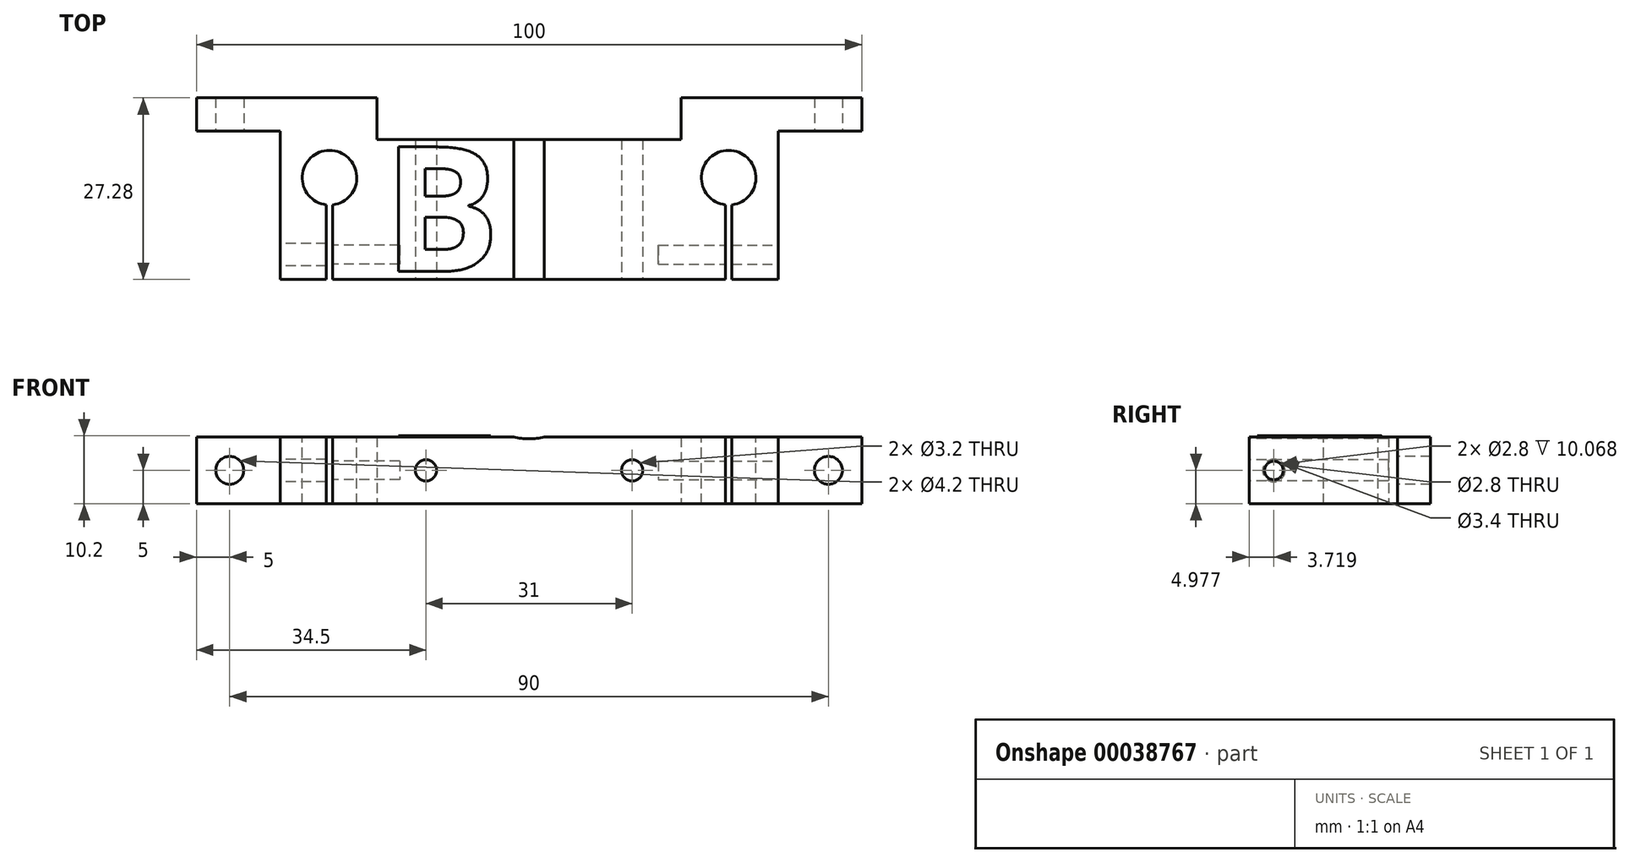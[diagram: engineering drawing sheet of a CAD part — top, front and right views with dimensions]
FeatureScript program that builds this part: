
annotation { "Feature Type Name" : "Feature", "Feature Type Description" : "" }
export const myFeature = defineFeature(function(context is Context, id is Id, definition is map)
    precondition{}
    {
        {
            var Q0;
            Q0=qCreatedBy(makeId("Top.planeOp"),FACE);
            var sketch = newSketch(context, id + "F0", { "sketchPlane" : qUnion([Q0])});
            skLineSegment(sketch, "E0", {"start": v(0, -13.82) * mm, "end": v(-37.44, -13.82) * mm});
            skLineSegment(sketch, "E1", {"start": v(-37.44, -13.82) * mm, "end": v(-37.44, 8.46) * mm});
            skLineSegment(sketch, "E2", {"start": v(-37.44, 8.46) * mm, "end": v(-50, 8.46) * mm});
            skLineSegment(sketch, "E3", {"start": v(-50, 8.46) * mm, "end": v(-50, 13.46) * mm});
            skLineSegment(sketch, "E4", {"start": v(-50, 13.46) * mm, "end": v(-22.87, 13.46) * mm});
            skLineSegment(sketch, "E5", {"start": v(-22.87, 13.46) * mm, "end": v(-22.87, 7.18) * mm});
            skLineSegment(sketch, "E6", {"start": v(-22.87, 7.18) * mm, "end": v(0, 7.18) * mm});
            skLineSegment(sketch, "E7", {"start": v(0, 7.18) * mm, "end": v(0, -13.82) * mm});
            skSolve(sketch);
        }
        {
            var Q0;
            Q0=qSketchRegion(id+"F0",true);
            extrude(context, id + "F1", {"entities" : qUnion([Q0]), "depth" : 10 * mm});
        }
        {
            var Q0;
            Q0=makeQuery(id+"F1.opExtrude","SWEPT_FACE",FACE,{"disambiguationData":[OSD([sQuery(id+"F0.wireOp",EDGE,"E0")])]});
            var sketch = newSketch(context, id + "F2", { "sketchPlane" : qUnion([Q0])});
            skLineSegment(sketch, "E8", {"start": v(0, 5) * mm, "end": v(0, 5) * mm});
            skCircle(sketch, "E9", {"center": v(-15.5, 5) * mm, "radius": 1.6 * mm});
            skCircle(sketch, "E10", {"center": v(0, 20.5) * mm, "radius": 10.75 * mm});
            skSolve(sketch);
        }
        {
            var Q0;
            Q0=qSketchRegion(id+"F2",true);
            extrude(context, id + "F3", {"entities" : qUnion([Q0]), "operationType" : NewBodyOperationType.REMOVE, "endBound" : BoundingType.THROUGH_ALL, "oppositeDirection" : true, "depth" : 25 * mm});
        }
        {
            var Q0;
            Q0=makeQuery(id+"F1.opExtrude","SWEPT_FACE",FACE,{"disambiguationData":[OSD([sQuery(id+"F0.wireOp",EDGE,"E2")])]});
            var sketch = newSketch(context, id + "F4", { "sketchPlane" : qUnion([Q0])});
            skLineSegment(sketch, "E11", {"start": v(-50, 5) * mm, "end": v(-37.44, 5) * mm, "construction": true});
            skLineSegment(sketch, "E12", {"start": v(-43.72, 10) * mm, "end": v(-43.72, 0) * mm, "construction": true});
            skCircle(sketch, "E13", {"center": v(-45, 5) * mm, "radius": 2.1 * mm});
            skSolve(sketch);
        }
        {
            var Q0;
            Q0=qSketchRegion(id+"F4",true);
            extrude(context, id + "F5", {"entities" : qUnion([Q0]), "operationType" : NewBodyOperationType.REMOVE, "endBound" : BoundingType.THROUGH_ALL, "oppositeDirection" : true, "depth" : 25 * mm});
        }
        {
            var Q0;
            {var subQ0=makeQuery(id+"F1.opExtrude","CAP_FACE",FACE,{"disambiguationData":[OSD([sQuery(id+"F0.wireOp",EDGE,"E0"),sQuery(id+"F0.wireOp",EDGE,"fd64a43a-5635-4f94-a977-4dd36923accb"),sQuery(id+"F0.wireOp",EDGE,"1334f7d4-4c90-4769-8fa3-fe5f576fb005"),sQuery(id+"F0.wireOp",EDGE,"E1"),sQuery(id+"F0.wireOp",EDGE,"E2"),sQuery(id+"F0.wireOp",EDGE,"E3"),sQuery(id+"F0.wireOp",EDGE,"E4"),sQuery(id+"F0.wireOp",EDGE,"E5"),sQuery(id+"F0.wireOp",EDGE,"E6"),sQuery(id+"F0.wireOp",EDGE,"E7")])],"isStart":false});Q0=makeQuery(id+"F10.boolean.opBoolean","MERGE",FACE,{"derivedFrom":[subQ0,makeQuery(id+"F10.opPattern","COPY",FACE,{"derivedFrom":subQ0,"instanceName":"1"})]});}
            var sketch = newSketch(context, id + "F6", { "sketchPlane" : qUnion([Q0])});
            skCircle(sketch, "E14", {"center": v(-30, 1.46) * mm, "radius": 4.1 * mm});
            skLineSegment(sketch, "E15", {"start": v(-30, 1.46) * mm, "end": v(-30, -13.82) * mm, "construction": true});
            skLineSegment(sketch, "E16.bottom", {"start": v(-30.49, -2.04) * mm, "end": v(-29.51, -2.04) * mm});
            skLineSegment(sketch, "E16.top", {"start": v(-30.49, -14.16) * mm, "end": v(-29.51, -14.16) * mm});
            skLineSegment(sketch, "E16.left", {"start": v(-30.49, -2.04) * mm, "end": v(-30.49, -14.16) * mm});
            skLineSegment(sketch, "E16.right", {"start": v(-29.51, -2.04) * mm, "end": v(-29.51, -14.16) * mm});
            skPoint(sketch, "E17", {"position": v(-30, -2.04) * mm});
            skSolve(sketch);
        }
        {
            var Q0;
            Q0=qSketchRegion(id+"F6",true);
            var Q1;
            {var subQ3=sQuery(id+"F6.wireOp",EDGE,"E16.bottom");Q1=makeQuery(id+"F6.imprint","IMPRINT",FACE,{"disambiguationData":[TD([[makeQuery(id+"F6.imprint","IMPRINT",EDGE,{"derivedFrom":subQ3}),-1.0]])]});}
            extrude(context, id + "F7", {"entities" : qUnion([Q0, Q1]), "operationType" : NewBodyOperationType.REMOVE, "endBound" : BoundingType.THROUGH_ALL, "oppositeDirection" : true, "depth" : 25 * mm});
        }
        {
            var Q0;
            Q0=makeQuery(id+"F1.opExtrude","SWEPT_FACE",FACE,{"disambiguationData":[OSD([sQuery(id+"F0.wireOp",EDGE,"E1")])]});
            var sketch = newSketch(context, id + "F8", { "sketchPlane" : qUnion([Q0])});
            skCircle(sketch, "E18", {"center": v(10.1, 4.98) * mm, "radius": 1.4 * mm});
            skCircle(sketch, "E19", {"center": v(10.1, 4.98) * mm, "radius": 1.7 * mm});
            skSolve(sketch);
        }
        {
            var Q0;
            Q0=makeQuery(id+"F8.imprint","IMPRINT",FACE,{"disambiguationData":[TD([[makeQuery(id+"F8.imprint","IMPRINT",EDGE,{"derivedFrom":sQuery(id+"F8.wireOp",EDGE,"E18")}),1.0]])]});
            extrude(context, id + "F9", {"entities" : qUnion([Q0]), "operationType" : NewBodyOperationType.REMOVE, "oppositeDirection" : true, "depth" : 18 * mm});
        }
        {
            var Q0;
            Q0=makeQuery(id+"F1.opExtrude","SWEPT_BODY",BODY,{"disambiguationData":[OSD([sQuery(id+"F0.wireOp",EDGE,"E0"),sQuery(id+"F0.wireOp",EDGE,"fd64a43a-5635-4f94-a977-4dd36923accb"),sQuery(id+"F0.wireOp",EDGE,"1334f7d4-4c90-4769-8fa3-fe5f576fb005"),sQuery(id+"F0.wireOp",EDGE,"E1"),sQuery(id+"F0.wireOp",EDGE,"E2"),sQuery(id+"F0.wireOp",EDGE,"E3"),sQuery(id+"F0.wireOp",EDGE,"E4"),sQuery(id+"F0.wireOp",EDGE,"E5"),sQuery(id+"F0.wireOp",EDGE,"E6"),sQuery(id+"F0.wireOp",EDGE,"E7")])]});
            var Q1;
            Q1=qCreatedBy(makeId("Right.planeOp"),FACE);
            mirror(context, id + "F10", {"operationType" : NewBodyOperationType.ADD, "entities" : qUnion([Q0]), "mirrorPlane" : qUnion([Q1])});
        }
        {
            var Q0;
            Q0=makeQuery(id+"F1.opExtrude","CAP_FACE",FACE,{"disambiguationData":[OSD([sQuery(id+"F0.wireOp",EDGE,"E0"),sQuery(id+"F0.wireOp",EDGE,"E1"),sQuery(id+"F0.wireOp",EDGE,"E2"),sQuery(id+"F0.wireOp",EDGE,"E3"),sQuery(id+"F0.wireOp",EDGE,"E4"),sQuery(id+"F0.wireOp",EDGE,"E5"),sQuery(id+"F0.wireOp",EDGE,"E6"),sQuery(id+"F0.wireOp",EDGE,"E7")])],"isStart":false});
            var sketch = newSketch(context, id + "F11", { "sketchPlane" : qUnion([Q0])});
            skText(sketch, "E20", { "text": "B", "fontName": "OpenSans-Bold.ttf"});
            const initialGuessF11  = {"E20": [-0.02198, -0.01261, 1, 0, 0.01886]};
            skSetInitialGuess(sketch, initialGuessF11);
            skSolve(sketch);
        }
        {
            var Q0;
            Q0=qSketchRegion(id+"F11",true);
            extrude(context, id + "F12", {"entities" : qUnion([Q0]), "operationType" : NewBodyOperationType.ADD, "depth" : .2 * mm});
        }
        {
            var Q0;
            Q0=makeQuery(id+"F8.imprint","IMPRINT",FACE,{"disambiguationData":[TD([[makeQuery(id+"F8.imprint","IMPRINT",EDGE,{"derivedFrom":sQuery(id+"F8.wireOp",EDGE,"E18")}),1.0]])]});
            var Q1;
            Q1=makeQuery(id+"F8.imprint","IMPRINT",FACE,{"disambiguationData":[TD([[makeQuery(id+"F8.imprint","IMPRINT",EDGE,{"derivedFrom":sQuery(id+"F8.wireOp",EDGE,"E18")}),-1.0]])]});
            extrude(context, id + "F13", {"entities" : qUnion([Q0, Q1]), "operationType" : NewBodyOperationType.REMOVE, "endBound" : BoundingType.UP_TO_NEXT, "oppositeDirection" : true, "depth" : 25 * mm});
        }
    });
